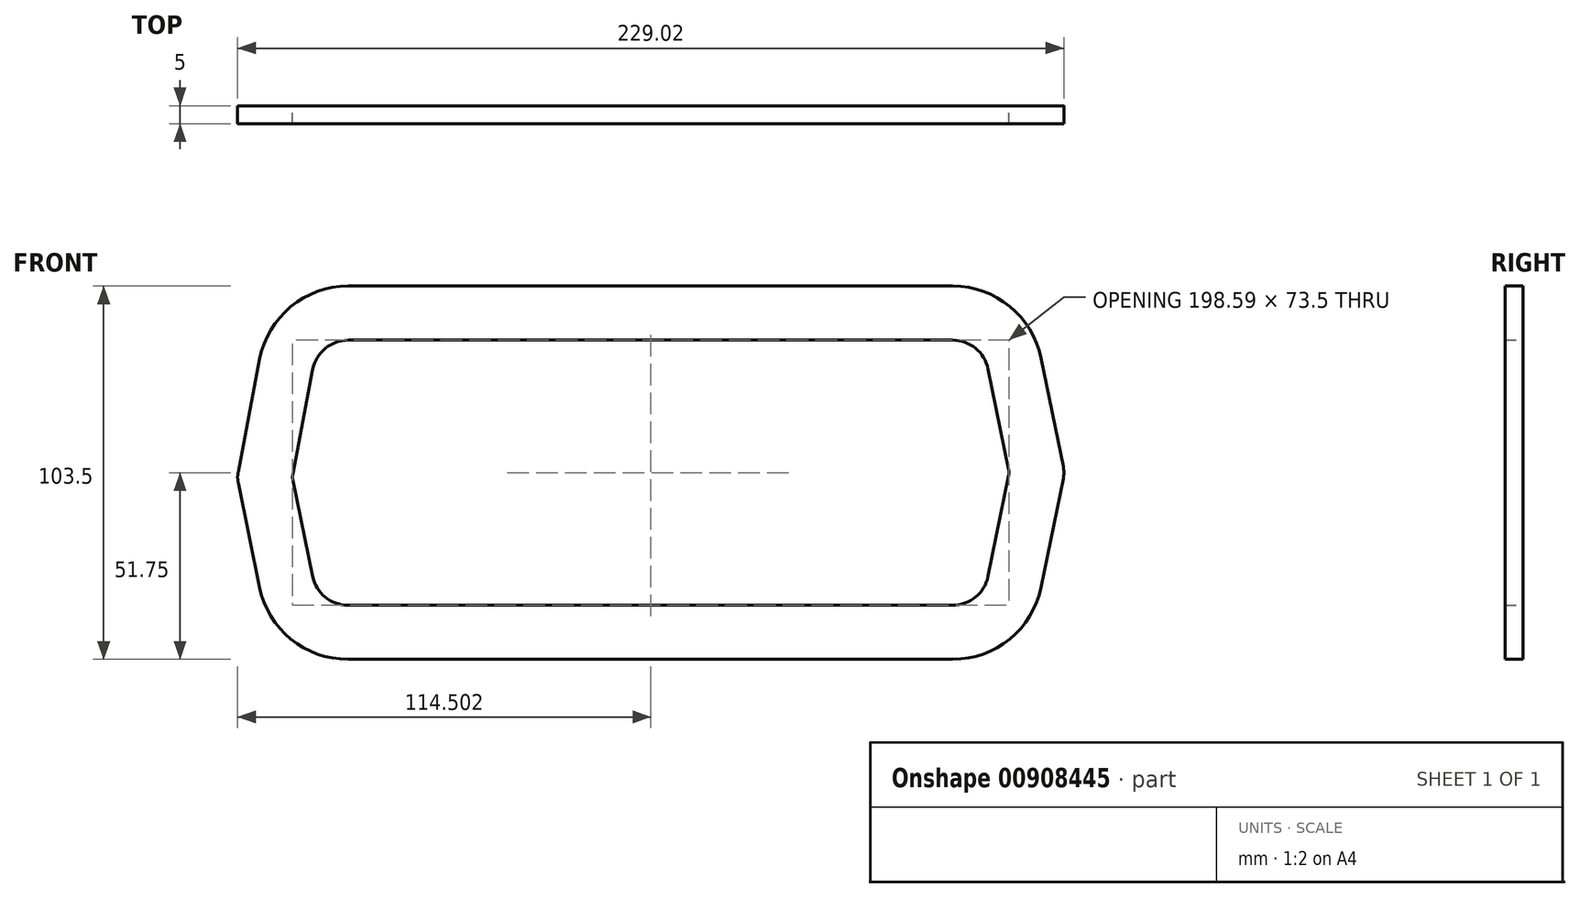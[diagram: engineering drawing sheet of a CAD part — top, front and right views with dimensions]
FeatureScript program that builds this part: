
annotation { "Feature Type Name" : "Feature", "Feature Type Description" : "" }
export const myFeature = defineFeature(function(context is Context, id is Id, definition is map)
    precondition{}
    {
        {
            var Q0;
            Q0=qCreatedBy(makeId("Front.planeOp"),FACE);
            var sketch = newSketch(context, id + "F0", { "sketchPlane" : qUnion([Q0])});
            skPoint(sketch, "E0.middle", {"position": v(0, 0) * mm});
            skLineSegment(sketch, "E1.bottom", {"start": v(83.83, 36.75) * mm, "end": v(-83.73, 36.75) * mm});
            skLineSegment(sketch, "E1.top", {"start": v(83.83, -36.75) * mm, "end": v(-83.83, -36.75) * mm});
            skPoint(sketch, "E2.endSnap0", {"position": v(-99.25, -1.23) * mm});
            skLineSegment(sketch, "E3", {"start": v(-99.1, -2) * mm, "end": v(-93.63, -28.75) * mm});
            skLineSegment(sketch, "E4", {"start": v(-93.55, 28.63) * mm, "end": v(-99.1, -0.45) * mm});
            skLineSegment(sketch, "E5", {"start": v(93.63, 28.75) * mm, "end": v(99.34, 0.8) * mm});
            skLineSegment(sketch, "E6", {"start": v(99.34, -0.8) * mm, "end": v(93.63, -28.75) * mm});
            skPoint(sketch, "E7.visualSharp", {"position": v(-92, 36.75) * mm});
            skArc(sketch, "E7.filletArc", {"start": v(-83.73, 36.75) * mm, "mid": v(-90.1, 34.46) * mm, "end": v(-93.55, 28.63) * mm});
            skPoint(sketch, "E8.visualSharp", {"position": v(-92, -36.75) * mm});
            skArc(sketch, "E8.filletArc", {"start": v(-93.63, -28.75) * mm, "mid": v(-90.16, -34.5) * mm, "end": v(-83.83, -36.75) * mm});
            skPoint(sketch, "E9.visualSharp", {"position": v(92, -36.75) * mm});
            skArc(sketch, "E9.filletArc", {"start": v(83.83, -36.75) * mm, "mid": v(90.16, -34.5) * mm, "end": v(93.63, -28.75) * mm});
            skPoint(sketch, "E10.visualSharp", {"position": v(92, 36.75) * mm});
            skArc(sketch, "E10.filletArc", {"start": v(93.63, 28.75) * mm, "mid": v(90.16, 34.5) * mm, "end": v(83.83, 36.75) * mm});
            skArc(sketch, "E11.filletArc", {"start": v(-99.1, -0.45) * mm, "mid": v(-99.17, -1.23) * mm, "end": v(-99.1, -2) * mm});
            skPoint(sketch, "E12.visualSharp", {"position": v(99.5, 0) * mm});
            skArc(sketch, "E12.filletArc", {"start": v(99.34, -0.8) * mm, "mid": v(99.42, 0) * mm, "end": v(99.34, 0.8) * mm});
            skLineSegment(sketch, "E13.0", {"start": v(83.83, 51.75) * mm, "end": v(-83.73, 51.75) * mm});
            skArc(sketch, "E13.1", {"start": v(108.33, 31.75) * mm, "mid": v(99.65, 46.11) * mm, "end": v(83.83, 51.75) * mm});
            skLineSegment(sketch, "E13.2", {"start": v(108.33, 31.75) * mm, "end": v(114.03, 3.8) * mm});
            skLineSegment(sketch, "E14.0", {"start": v(83.83, -51.75) * mm, "end": v(-83.83, -51.75) * mm});
            skArc(sketch, "E14.1", {"start": v(83.83, -51.75) * mm, "mid": v(99.65, -46.11) * mm, "end": v(108.33, -31.75) * mm});
            skLineSegment(sketch, "E14.2", {"start": v(114.03, -3.8) * mm, "end": v(108.33, -31.75) * mm});
            skLineSegment(sketch, "E15.0", {"start": v(-108.28, 31.44) * mm, "end": v(-113.84, 2.36) * mm});
            skArc(sketch, "E15.1", {"start": v(-83.73, 51.75) * mm, "mid": v(-99.66, 46.01) * mm, "end": v(-108.28, 31.44) * mm});
            skLineSegment(sketch, "E16.0", {"start": v(-113.79, -5) * mm, "end": v(-108.33, -31.75) * mm});
            skArc(sketch, "E17.0", {"start": v(-108.33, -31.75) * mm, "mid": v(-99.65, -46.11) * mm, "end": v(-83.83, -51.75) * mm});
            skLineSegment(sketch, "E18", {"start": v(-108.33, -31.75) * mm, "end": v(-114.22, -2.87) * mm});
            skLineSegment(sketch, "E19", {"start": v(-108.28, 31.44) * mm, "end": v(-114.24, 0.23) * mm});
            skArc(sketch, "E20.filletArc", {"start": v(-114.24, 0.23) * mm, "mid": v(-114.38, -1.32) * mm, "end": v(-114.22, -2.87) * mm});
            skLineSegment(sketch, "E21", {"start": v(109.97, 23.7) * mm, "end": v(114.48, 1.6) * mm});
            skLineSegment(sketch, "E22", {"start": v(108.33, -31.75) * mm, "end": v(114.48, -1.6) * mm});
            skArc(sketch, "E23.filletArc", {"start": v(114.48, -1.6) * mm, "mid": v(114.64, 0) * mm, "end": v(114.48, 1.6) * mm});
            skSolve(sketch);
        }
        {
            var Q0;
            Q0=makeQuery(id+"F0.imprint","IMPRINT",FACE,{"disambiguationData":[TD([[makeQuery(id+"F0.imprint","IMPRINT",EDGE,{"derivedFrom":sQuery(id+"F0.wireOp",EDGE,"E1.bottom")}),-1.0]])]});
            extrude(context, id + "F1", {"entities" : qUnion([Q0]), "depth" : 5 * mm, "offsetDistance" : 25 * mm});
        }
    });
